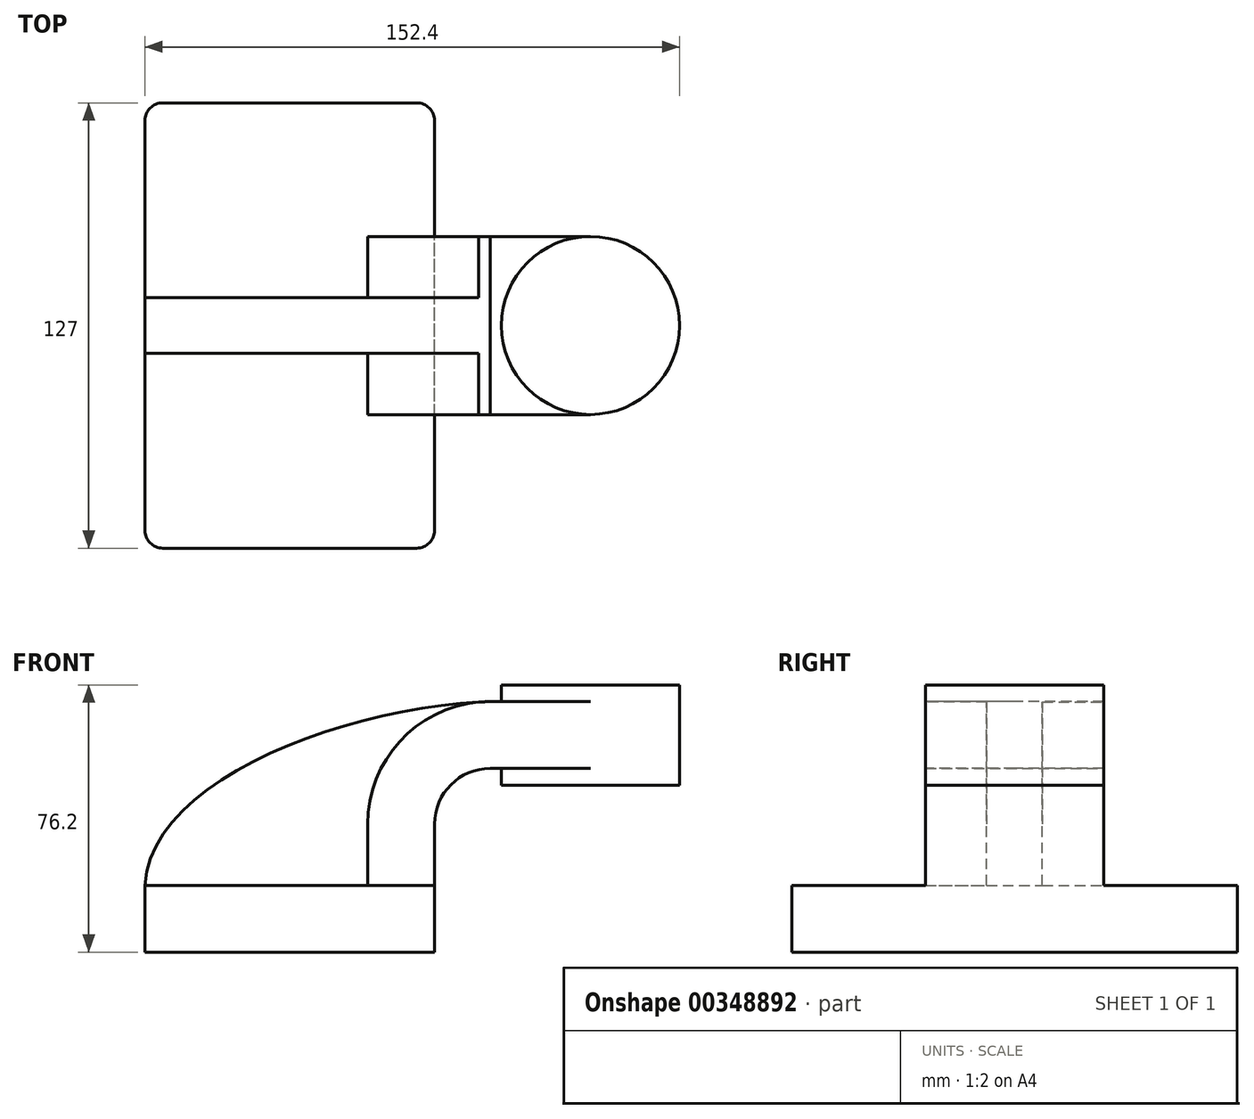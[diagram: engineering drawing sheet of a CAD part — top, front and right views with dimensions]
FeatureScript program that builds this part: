
annotation { "Feature Type Name" : "Feature", "Feature Type Description" : "" }
export const myFeature = defineFeature(function(context is Context, id is Id, definition is map)
    precondition{}
    {
        {
            var Q0;
            Q0=qCreatedBy(makeId("Front.planeOp"),FACE);
            var sketch = newSketch(context, id + "F0", { "sketchPlane" : qUnion([Q0])});
            skLineSegment(sketch, "E0.rect.bottom", {"start": v(-133.9, 11.82) * mm, "end": v(-51.36, 11.82) * mm});
            skLineSegment(sketch, "E0.rect.top", {"start": v(-133.9, -7.23) * mm, "end": v(-51.36, -7.23) * mm});
            skLineSegment(sketch, "E0.rect.left", {"start": v(-133.9, 11.82) * mm, "end": v(-133.9, -7.23) * mm});
            skLineSegment(sketch, "E0.rect.right", {"start": v(-51.36, 11.82) * mm, "end": v(-51.36, -7.23) * mm});
            skPoint(sketch, "E0.rect.middle", {"position": v(-92.63, 2.3) * mm});
            skLineSegment(sketch, "E1", {"start": v(-51.36, 11.82) * mm, "end": v(-51.36, 29.3) * mm});
            skArc(sketch, "E2", {"start": v(-51.36, 29.3) * mm, "mid": v(-46.71, 40.52) * mm, "end": v(-35.48, 45.17) * mm});
            skLineSegment(sketch, "E3", {"start": v(-35.48, 45.17) * mm, "end": v(-6.9, 45.17) * mm});
            skLineSegment(sketch, "E4.rect.bottom", {"start": v(-32.3, 40.4) * mm, "end": v(18.5, 40.4) * mm});
            skLineSegment(sketch, "E4.rect.top", {"start": v(-32.3, 68.97) * mm, "end": v(18.5, 68.97) * mm});
            skLineSegment(sketch, "E4.rect.left", {"start": v(-32.3, 40.4) * mm, "end": v(-32.3, 68.97) * mm});
            skLineSegment(sketch, "E4.rect.right", {"start": v(18.5, 40.4) * mm, "end": v(18.5, 68.97) * mm});
            skPoint(sketch, "E4.rect.middle", {"position": v(-6.9, 54.68) * mm});
            skLineSegment(sketch, "E5.0", {"start": v(-35.48, 64.22) * mm, "end": v(-6.9, 64.22) * mm});
            skArc(sketch, "E5.1", {"start": v(-70.4, 29.3) * mm, "mid": v(-60.18, 53.99) * mm, "end": v(-35.48, 64.22) * mm});
            skLineSegment(sketch, "E5.2", {"start": v(-70.4, 11.82) * mm, "end": v(-70.4, 29.3) * mm});
            skLineSegment(sketch, "E6", {"start": v(-6.9, 40.4) * mm, "end": v(-6.9, 68.97) * mm});
            skFitSpline(sketch, "E7", {"points": [v(-133.9, 11.82) * mm, v(-35.48, 64.22) * mm], "startDerivative": vector(5.2, 92.34) * mm, "endDerivative": vector(120.92, 4.22) * mm});
            skSolve(sketch);
        }
        {
            var Q0;
            Q0=makeQuery(id+"F0.imprint","IMPRINT",FACE,{"disambiguationData":[TD([[makeQuery(id+"F0.imprint","IMPRINT",EDGE,{"derivedFrom":sQuery(id+"F0.wireOp",EDGE,"E0.rect.top")}),1.0]])]});
            extrude(context, id + "F1", {"entities" : qUnion([Q0]), "endBound" : BoundingType.SYMMETRIC, "depth" : 127 * mm});
        }
        {
            var Q0;
            {var subQ4=sQuery(id+"F0.wireOp",EDGE,"E1");Q0=makeQuery(id+"F0.imprint","IMPRINT",FACE,{"disambiguationData":[TD([[makeQuery(id+"F0.imprint","IMPRINT",EDGE,{"derivedFrom":subQ4}),1.0]])]});}
            var Q1;
            {var subQ0=sQuery(id+"F0.wireOp",EDGE,"E6");var subQ1=sQuery(id+"F0.wireOp",EDGE,"E3");var subQ2=makeQuery(id+"F0.imprint","INTERSECT",VERTEX,{"derivedFrom":[subQ1,subQ0]});Q1=makeQuery(id+"F0.imprint","IMPRINT",FACE,{"disambiguationData":[TD([[makeQuery(id+"F0.imprint","IMPRINT",EDGE,{"disambiguationData":[TD([[subQ2,1.0]])],"derivedFrom":subQ1}),1.0]])]});}
            extrude(context, id + "F2", {"entities" : qUnion([Q0, Q1]), "operationType" : NewBodyOperationType.ADD, "endBound" : BoundingType.SYMMETRIC, "depth" : 50.8 * mm});
        }
        {
            var Q0;
            {var subQ3=sQuery(id+"F0.wireOp",EDGE,"E5.2");Q0=makeQuery(id+"F0.imprint","IMPRINT",FACE,{"disambiguationData":[TD([[makeQuery(id+"F0.imprint","IMPRINT",EDGE,{"derivedFrom":subQ3}),1.0]])]});}
            extrude(context, id + "F3", {"entities" : qUnion([Q0]), "operationType" : NewBodyOperationType.ADD, "endBound" : BoundingType.SYMMETRIC, "depth" : 15.88 * mm});
        }
        {
            var Q0;
            {var subQ0=sQuery(id+"F0.wireOp",EDGE,"E4.rect.right");Q0=makeQuery(id+"F0.imprint","IMPRINT",FACE,{"disambiguationData":[TD([[makeQuery(id+"F0.imprint","IMPRINT",EDGE,{"derivedFrom":subQ0}),1.0]])]});}
            var Q1;
            Q1=sQuery(id+"F0.wireOp",EDGE,"E6");
            revolve(context, id + "F4", {"operationType" : NewBodyOperationType.ADD, "entities" : qUnion([Q0]), "axis" : qUnion([Q1]), "revolveType" : RevolveType.FULL});
        }
        {
            var Q0;
            Q0=makeQuery(id+"F1.opExtrude","CAP_EDGE",EDGE,{"disambiguationData":[OSD([sQuery(id+"F0.wireOp",EDGE,"E0.rect.right")])],"isStart":false});
            var Q1;
            Q1=makeQuery(id+"F1.opExtrude","CAP_EDGE",EDGE,{"disambiguationData":[OSD([sQuery(id+"F0.wireOp",EDGE,"E0.rect.left")])],"isStart":false});
            var Q2;
            Q2=makeQuery(id+"F1.opExtrude","CAP_EDGE",EDGE,{"disambiguationData":[OSD([sQuery(id+"F0.wireOp",EDGE,"E0.rect.left")])],"isStart":true});
            var Q3;
            Q3=makeQuery(id+"F1.opExtrude","CAP_EDGE",EDGE,{"disambiguationData":[OSD([sQuery(id+"F0.wireOp",EDGE,"E0.rect.right")])],"isStart":true});
            fillet(context, id + "F5", {"entities" : qUnion([Q0, Q1, Q2, Q3]), "radius" : 5.08 * mm, "tangentPropagation" : true, "allowEdgeOverflow" : false});
        }
    });
